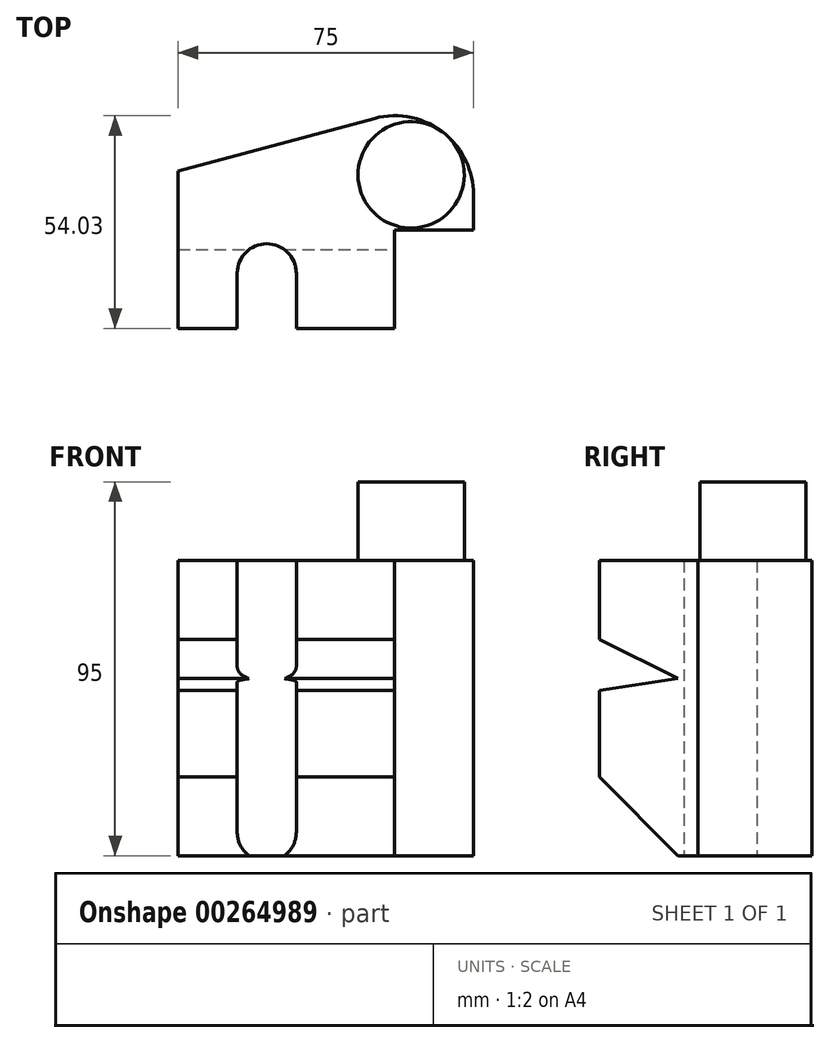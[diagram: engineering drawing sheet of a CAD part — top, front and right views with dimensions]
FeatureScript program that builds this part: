
annotation { "Feature Type Name" : "Feature", "Feature Type Description" : "" }
export const myFeature = defineFeature(function(context is Context, id is Id, definition is map)
    precondition{}
    {
        {
            var Q0;
            Q0=qCreatedBy(makeId("Top.planeOp"),FACE);
            var sketch = newSketch(context, id + "F0", { "sketchPlane" : qUnion([Q0])});
            skLineSegment(sketch, "E0", {"start": v(0, 0) * mm, "end": v(15, 0) * mm});
            skLineSegment(sketch, "E1", {"start": v(15, 0) * mm, "end": v(15, 14) * mm});
            skLineSegment(sketch, "E2", {"start": v(0, 0) * mm, "end": v(0, 40) * mm});
            skLineSegment(sketch, "E3", {"start": v(30, 14) * mm, "end": v(30, 0) * mm});
            skLineSegment(sketch, "E4", {"start": v(30, 0) * mm, "end": v(55, 0) * mm});
            skLineSegment(sketch, "E5", {"start": v(55, 0) * mm, "end": v(55, 25) * mm});
            skLineSegment(sketch, "E6", {"start": v(55, 25) * mm, "end": v(75, 25) * mm});
            skLineSegment(sketch, "E7", {"start": v(75, 25) * mm, "end": v(75, 34.03) * mm});
            skArc(sketch, "E8", {"start": v(15, 14) * mm, "mid": v(22.5, 21.5) * mm, "end": v(30, 14) * mm});
            skLineSegment(sketch, "E9", {"start": v(0, 40) * mm, "end": v(49.82, 53.35) * mm});
            skArc(sketch, "E10", {"start": v(75, 34.03) * mm, "mid": v(67.18, 49.9) * mm, "end": v(49.82, 53.35) * mm});
            skSolve(sketch);
        }
        {
            var Q0;
            Q0=makeQuery(id+"F0.imprint","IMPRINT",FACE,{"disambiguationData":[TD([[makeQuery(id+"F0.imprint","IMPRINT",EDGE,{"derivedFrom":sQuery(id+"F0.wireOp",EDGE,"E0")}),1.0]])]});
            extrude(context, id + "F1", {"entities" : qUnion([Q0]), "depth" : 75 * mm});
        }
        {
            var Q0;
            Q0=makeQuery(id+"F1.opExtrude","SWEPT_FACE",FACE,{"disambiguationData":[OSD([sQuery(id+"F0.wireOp",EDGE,"E5")])]});
            var sketch = newSketch(context, id + "F2", { "sketchPlane" : qUnion([Q0])});
            skLineSegment(sketch, "E11", {"start": v(0, 0) * mm, "end": v(0, 20) * mm});
            skLineSegment(sketch, "E12", {"start": v(0, 0) * mm, "end": v(20, 0) * mm});
            skLineSegment(sketch, "E13", {"start": v(20, 0) * mm, "end": v(0, 20) * mm});
            skSolve(sketch);
        }
        {
            var Q0;
            Q0 = qSketchRegion(id + "F2", true);
            extrude(context, id + "F3", {"entities" : qUnion([Q0]), "operationType" : NewBodyOperationType.REMOVE, "endBound" : BoundingType.SYMMETRIC, "oppositeDirection" : true, "depth" : 200 * mm});
        }
        {
            var Q0;
            Q0=makeQuery(id+"F1.opExtrude","SWEPT_FACE",FACE,{"disambiguationData":[OSD([sQuery(id+"F0.wireOp",EDGE,"E5")])]});
            var sketch = newSketch(context, id + "F4", { "sketchPlane" : qUnion([Q0])});
            skLineSegment(sketch, "E14", {"start": v(20, 45) * mm, "end": v(0, 55) * mm});
            skLineSegment(sketch, "E15", {"start": v(0, 55) * mm, "end": v(0, 42.03) * mm});
            skLineSegment(sketch, "E16", {"start": v(0, 42.03) * mm, "end": v(20, 45) * mm});
            skSolve(sketch);
        }
        {
            var Q0;
            Q0=makeQuery(id+"F4.imprint","IMPRINT",FACE,{"disambiguationData":[TD([[makeQuery(id+"F4.imprint","IMPRINT",EDGE,{"derivedFrom":sQuery(id+"F4.wireOp",EDGE,"E14")}),1.0]])]});
            extrude(context, id + "F5", {"entities" : qUnion([Q0]), "operationType" : NewBodyOperationType.REMOVE, "oppositeDirection" : true, "depth" : 100 * mm});
        }
        {
            var Q0;
            Q0=makeQuery(id+"F1.opExtrude","CAP_FACE",FACE,{"disambiguationData":[OSD([sQuery(id+"F0.wireOp",EDGE,"E0"),sQuery(id+"F0.wireOp",EDGE,"E1"),sQuery(id+"F0.wireOp",EDGE,"E2"),sQuery(id+"F0.wireOp",EDGE,"E3"),sQuery(id+"F0.wireOp",EDGE,"E4"),sQuery(id+"F0.wireOp",EDGE,"E5"),sQuery(id+"F0.wireOp",EDGE,"E6"),sQuery(id+"F0.wireOp",EDGE,"E7"),sQuery(id+"F0.wireOp",EDGE,"E8"),sQuery(id+"F0.wireOp",EDGE,"E9"),sQuery(id+"F0.wireOp",EDGE,"E10")])],"isStart":false});
            var sketch = newSketch(context, id + "F6", { "sketchPlane" : qUnion([Q0])});
            skCircle(sketch, "E17", {"center": v(59.2, 39) * mm, "radius": 13.5 * mm});
            skSolve(sketch);
        }
        {
            var Q0;
            Q0 = qSketchRegion(id + "F6", true);
            extrude(context, id + "F7", {"entities" : qUnion([Q0]), "operationType" : NewBodyOperationType.ADD, "depth" : 20 * mm});
        }
    });
